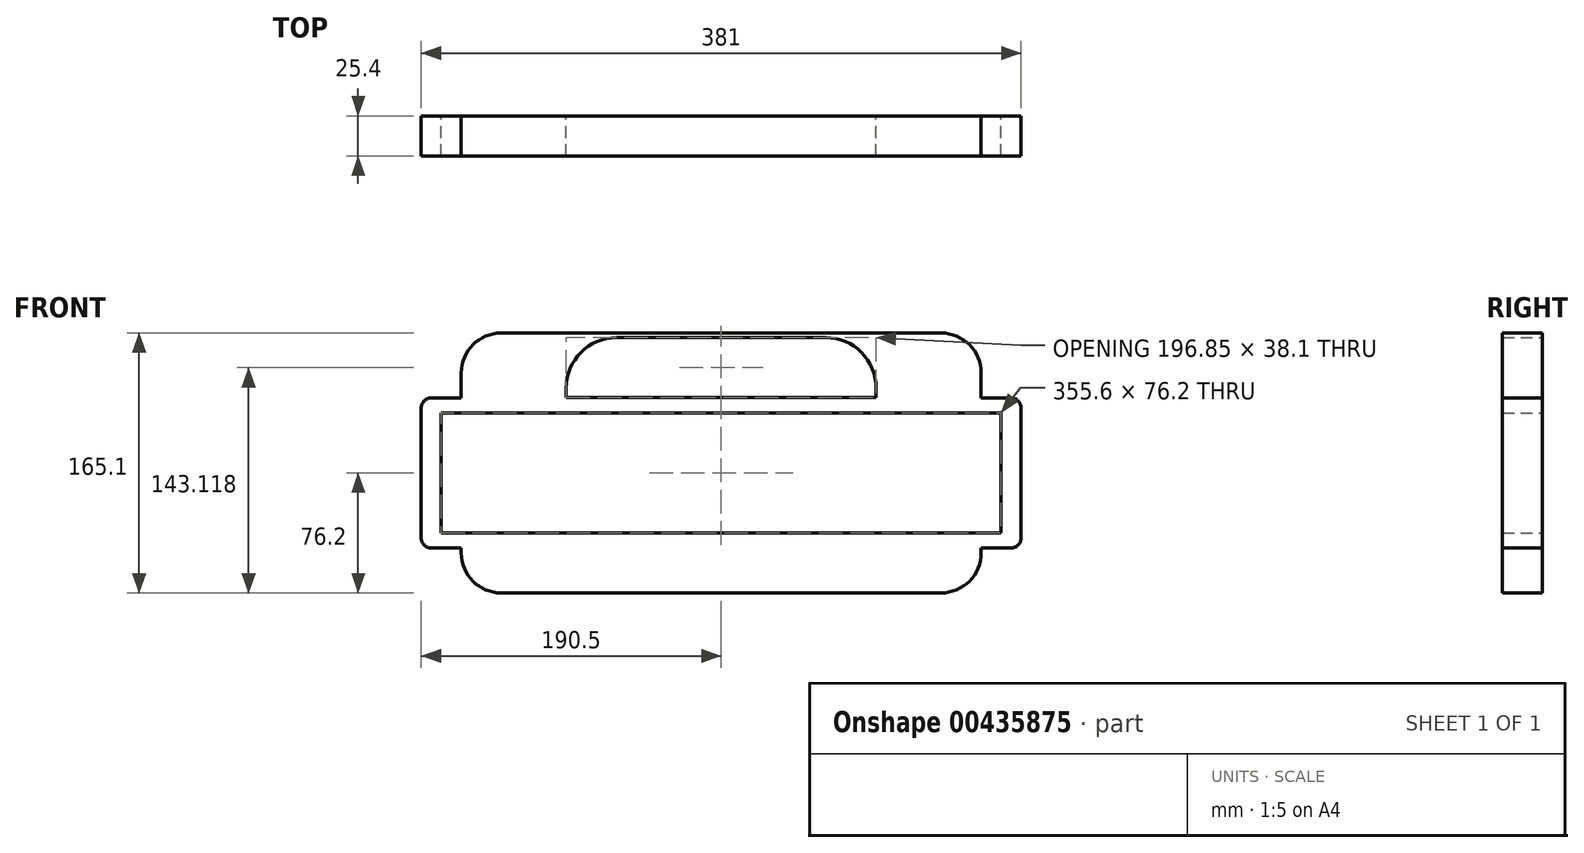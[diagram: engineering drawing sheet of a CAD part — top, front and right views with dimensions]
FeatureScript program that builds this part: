
annotation { "Feature Type Name" : "Feature", "Feature Type Description" : "" }
export const myFeature = defineFeature(function(context is Context, id is Id, definition is map)
    precondition{}
    {
        {
            var Q0;
            Q0=qCreatedBy(makeId("Front.planeOp"),FACE);
            var sketch = newSketch(context, id + "F0", { "sketchPlane" : qUnion([Q0])});
            skLineSegment(sketch, "E0.bottom", {"start": v(190.5, -47.63) * mm, "end": v(-190.5, -47.63) * mm});
            skLineSegment(sketch, "E0.top", {"start": v(190.5, 47.63) * mm, "end": v(-190.5, 47.63) * mm});
            skLineSegment(sketch, "E0.left", {"start": v(190.5, -47.63) * mm, "end": v(190.5, 47.63) * mm});
            skLineSegment(sketch, "E0.right", {"start": v(-190.5, -47.63) * mm, "end": v(-190.5, 47.63) * mm});
            skPoint(sketch, "E0.middle", {"position": v(0, 0) * mm});
            skLineSegment(sketch, "E1.bottom", {"start": v(177.8, -38.1) * mm, "end": v(-177.8, -38.1) * mm});
            skLineSegment(sketch, "E1.top", {"start": v(177.8, 38.1) * mm, "end": v(-177.8, 38.1) * mm});
            skLineSegment(sketch, "E1.left", {"start": v(177.8, -38.1) * mm, "end": v(177.8, 38.1) * mm});
            skLineSegment(sketch, "E1.right", {"start": v(-177.8, -38.1) * mm, "end": v(-177.8, 38.1) * mm});
            skLineSegment(sketch, "E2.bottom", {"start": v(98.43, 85.97) * mm, "end": v(-98.42, 85.97) * mm});
            skLineSegment(sketch, "E2.top", {"start": v(98.43, 47.87) * mm, "end": v(-98.43, 47.87) * mm});
            skLineSegment(sketch, "E2.left", {"start": v(98.43, 85.97) * mm, "end": v(98.43, 47.87) * mm});
            skLineSegment(sketch, "E2.right", {"start": v(-98.42, 85.97) * mm, "end": v(-98.42, 47.87) * mm});
            skPoint(sketch, "E2.middle", {"position": v(0, 66.92) * mm});
            skLineSegment(sketch, "E3.bottom", {"start": v(165.1, 88.9) * mm, "end": v(-165.1, 88.9) * mm});
            skLineSegment(sketch, "E3.top", {"start": v(165.1, -76.2) * mm, "end": v(-165.1, -76.2) * mm});
            skLineSegment(sketch, "E3.left", {"start": v(165.1, 88.9) * mm, "end": v(165.1, -76.2) * mm});
            skLineSegment(sketch, "E3.right", {"start": v(-165.1, 88.9) * mm, "end": v(-165.1, -76.2) * mm});
            skPoint(sketch, "E3.middle", {"position": v(0, 6.35) * mm});
            skArc(sketch, "E4", {"start": v(-66.43, 85.97) * mm, "mid": v(-89.05, 76.6) * mm, "end": v(-98.42, 53.98) * mm});
            skArc(sketch, "E5", {"start": v(98.43, 53.98) * mm, "mid": v(89.05, 76.6) * mm, "end": v(66.43, 85.97) * mm});
            skSolve(sketch);
        }
        {
            var Q0;
            {var subQ2=sQuery(id+"F0.wireOp",EDGE,"E2.top");Q0=makeQuery(id+"F0.imprint","IMPRINT",FACE,{"disambiguationData":[TD([[makeQuery(id+"F0.imprint","IMPRINT",EDGE,{"derivedFrom":subQ2}),1.0]])]});}
            var Q1;
            {var subQ3=sQuery(id+"F0.wireOp",EDGE,"E4");Q1=makeQuery(id+"F0.imprint","IMPRINT",FACE,{"disambiguationData":[TD([[makeQuery(id+"F0.imprint","IMPRINT",EDGE,{"derivedFrom":subQ3}),-1.0]])]});}
            var Q2;
            {var subQ3=sQuery(id+"F0.wireOp",EDGE,"E5");Q2=makeQuery(id+"F0.imprint","IMPRINT",FACE,{"disambiguationData":[TD([[makeQuery(id+"F0.imprint","IMPRINT",EDGE,{"derivedFrom":subQ3}),-1.0]])]});}
            var Q3;
            {var subQ8=sQuery(id+"F0.wireOp",EDGE,"E0.right");Q3=makeQuery(id+"F0.imprint","IMPRINT",FACE,{"disambiguationData":[TD([[makeQuery(id+"F0.imprint","IMPRINT",EDGE,{"derivedFrom":subQ8}),-1.0]])]});}
            var Q4;
            {var subQ0=sQuery(id+"F0.wireOp",EDGE,"E3.left");var subQ1=sQuery(id+"F0.wireOp",EDGE,"E0.top");var subQ2=makeQuery(id+"F0.imprint","INTERSECT",VERTEX,{"derivedFrom":[subQ1,subQ0]});Q4=makeQuery(id+"F0.imprint","IMPRINT",FACE,{"disambiguationData":[TD([[makeQuery(id+"F0.imprint","IMPRINT",EDGE,{"disambiguationData":[TD([[subQ2,-1.0]])],"derivedFrom":subQ1}),1.0]])]});}
            var Q5;
            {var subQ0=sQuery(id+"F0.wireOp",EDGE,"E0.left");Q5=makeQuery(id+"F0.imprint","IMPRINT",FACE,{"disambiguationData":[TD([[makeQuery(id+"F0.imprint","IMPRINT",EDGE,{"derivedFrom":subQ0}),1.0]])]});}
            var Q6;
            {var subQ0=sQuery(id+"F0.wireOp",EDGE,"E3.left");var subQ1=sQuery(id+"F0.wireOp",EDGE,"E0.bottom");var subQ2=makeQuery(id+"F0.imprint","INTERSECT",VERTEX,{"derivedFrom":[subQ1,subQ0]});Q6=makeQuery(id+"F0.imprint","IMPRINT",FACE,{"disambiguationData":[TD([[makeQuery(id+"F0.imprint","IMPRINT",EDGE,{"disambiguationData":[TD([[subQ2,-1.0]])],"derivedFrom":subQ1}),-1.0]])]});}
            var Q7;
            {var subQ5=sQuery(id+"F0.wireOp",EDGE,"E3.top");Q7=makeQuery(id+"F0.imprint","IMPRINT",FACE,{"disambiguationData":[TD([[makeQuery(id+"F0.imprint","IMPRINT",EDGE,{"derivedFrom":subQ5}),-1.0]])]});}
            extrude(context, id + "F1", {"entities" : qUnion([Q0, Q1, Q2, Q3, Q4, Q5, Q6, Q7]), "depth" : 25.4 * mm});
        }
        {
            var Q0;
            Q0=makeQuery(id+"F1.opExtrude","SWEPT_EDGE",EDGE,{"disambiguationData":[OSD([sQuery(id+"F0.wireOp",EDGE,"E3.bottom"),sQuery(id+"F0.wireOp",EDGE,"E3.right")])]});
            var Q1;
            Q1=makeQuery(id+"F1.opExtrude","SWEPT_EDGE",EDGE,{"disambiguationData":[OSD([sQuery(id+"F0.wireOp",EDGE,"E3.bottom"),sQuery(id+"F0.wireOp",EDGE,"E3.left")])]});
            var Q2;
            Q2=makeQuery(id+"F1.opExtrude","SWEPT_EDGE",EDGE,{"disambiguationData":[OSD([sQuery(id+"F0.wireOp",EDGE,"E3.top"),sQuery(id+"F0.wireOp",EDGE,"E3.right")])]});
            var Q3;
            Q3=makeQuery(id+"F1.opExtrude","SWEPT_EDGE",EDGE,{"disambiguationData":[OSD([sQuery(id+"F0.wireOp",EDGE,"E3.top"),sQuery(id+"F0.wireOp",EDGE,"E3.left")])]});
            fillet(context, id + "F2", {"entities" : qUnion([Q0, Q1, Q2, Q3]), "radius" : 25.4 * mm, "tangentPropagation" : true, "allowEdgeOverflow" : false});
        }
        {
            var Q0;
            Q0=makeQuery(id+"F1.opExtrude","SWEPT_EDGE",EDGE,{"disambiguationData":[OSD([sQuery(id+"F0.wireOp",EDGE,"E0.top"),sQuery(id+"F0.wireOp",EDGE,"E0.right")])]});
            var Q1;
            Q1=makeQuery(id+"F1.opExtrude","SWEPT_EDGE",EDGE,{"disambiguationData":[OSD([sQuery(id+"F0.wireOp",EDGE,"E0.bottom"),sQuery(id+"F0.wireOp",EDGE,"E0.right")])]});
            var Q2;
            Q2=makeQuery(id+"F1.opExtrude","SWEPT_EDGE",EDGE,{"disambiguationData":[OSD([sQuery(id+"F0.wireOp",EDGE,"E0.bottom"),sQuery(id+"F0.wireOp",EDGE,"E0.left")])]});
            var Q3;
            Q3=makeQuery(id+"F1.opExtrude","SWEPT_EDGE",EDGE,{"disambiguationData":[OSD([sQuery(id+"F0.wireOp",EDGE,"E0.top"),sQuery(id+"F0.wireOp",EDGE,"E0.left")])]});
            fillet(context, id + "F3", {"entities" : qUnion([Q0, Q1, Q2, Q3]), "radius" : 6.35 * mm, "tangentPropagation" : true, "allowEdgeOverflow" : false});
        }
    });
